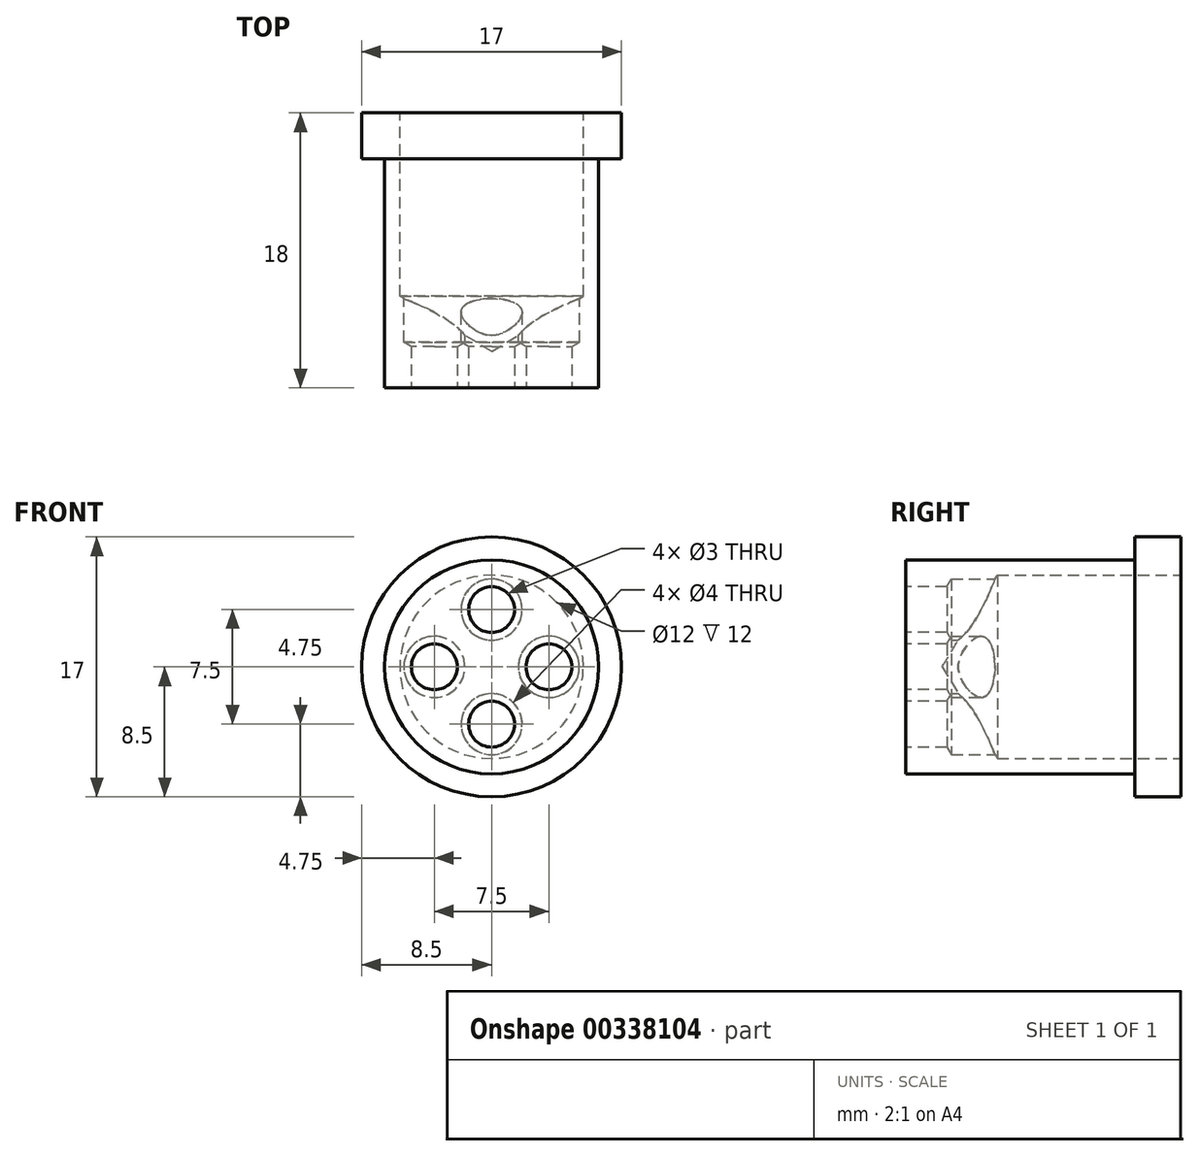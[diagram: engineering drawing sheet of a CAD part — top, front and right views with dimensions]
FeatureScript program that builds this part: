
annotation { "Feature Type Name" : "Feature", "Feature Type Description" : "" }
export const myFeature = defineFeature(function(context is Context, id is Id, definition is map)
    precondition{}
    {
        {
            var Q0;
            Q0=qCreatedBy(makeId("Front.planeOp"),FACE);
            var sketch = newSketch(context, id + "F0", { "sketchPlane" : qUnion([Q0])});
            skCircle(sketch, "E0", {"center": v(0, 0) * mm, "radius": 8.5 * mm});
            skSolve(sketch);
        }
        {
            var Q0;
            Q0=makeQuery(id+"F0.imprint","IMPRINT",FACE,{"disambiguationData":[TD([[makeQuery(id+"F0.imprint","IMPRINT",EDGE,{"derivedFrom":sQuery(id+"F0.wireOp",EDGE,"E0")}),1.0]])]});
            extrude(context, id + "F1", {"entities" : qUnion([Q0]), "depth" : 3 * mm});
        }
        {
            var Q0;
            Q0=makeQuery(id+"F1.opExtrude","CAP_FACE",FACE,{"disambiguationData":[OSD([sQuery(id+"F0.wireOp",EDGE,"E0")])],"isStart":false});
            var sketch = newSketch(context, id + "F2", { "sketchPlane" : qUnion([Q0])});
            skCircle(sketch, "E1", {"center": v(0, 0) * mm, "radius": 7 * mm});
            skSolve(sketch);
        }
        {
            var Q0;
            Q0=makeQuery(id+"F2.imprint","IMPRINT",FACE,{"disambiguationData":[TD([[makeQuery(id+"F2.imprint","IMPRINT",EDGE,{"derivedFrom":sQuery(id+"F2.wireOp",EDGE,"E1")}),1.0]])]});
            extrude(context, id + "F3", {"entities" : qUnion([Q0]), "operationType" : NewBodyOperationType.ADD, "depth" : 15 * mm});
        }
        {
            var Q0;
            Q0=makeQuery(id+"F3.opExtrude","CAP_FACE",FACE,{"disambiguationData":[OSD([sQuery(id+"F2.wireOp",EDGE,"E1")])],"isStart":false});
            var sketch = newSketch(context, id + "F4", { "sketchPlane" : qUnion([Q0])});
            skCircle(sketch, "E2", {"center": v(0, 3.75) * mm, "radius": 1.5 * mm});
            skCircle(sketch, "E3", {"center": v(-3.75, 0) * mm, "radius": 1.5 * mm});
            skCircle(sketch, "E4", {"center": v(0, -3.75) * mm, "radius": 1.5 * mm});
            skCircle(sketch, "E5", {"center": v(3.75, 0) * mm, "radius": 1.5 * mm});
            skSolve(sketch);
        }
        {
            var Q0;
            Q0=sQuery(id+"F4.wireOp",VERTEX,"E2.center");
            var Q1;
            Q1=sQuery(id+"F4.wireOp",VERTEX,"E5.center");
            var Q2;
            Q2=sQuery(id+"F4.wireOp",VERTEX,"E4.center");
            var Q3;
            Q3=sQuery(id+"F4.wireOp",VERTEX,"E3.center");
            var Q4;
            Q4=makeQuery(id+"F1.opExtrude","SWEPT_BODY",BODY,{"disambiguationData":[OSD([sQuery(id+"F0.wireOp",EDGE,"E0")])]});
            hole(context, id + "F5", {"style" : HoleStyle.SIMPLE, "endStyle" : HoleEndStyle.THROUGH, "holeDiameter" : 3 * mm, "tappedDepth" : 12 * mm, "tapClearance" : 3, "locations" : qUnion([Q0, Q1, Q2, Q3]), "scope" : qUnion([Q4])});
        }
        {
            var Q0;
            Q0=makeQuery(id+"F1.opExtrude","CAP_FACE",FACE,{"disambiguationData":[OSD([sQuery(id+"F0.wireOp",EDGE,"E0")])],"isStart":true});
            var sketch = newSketch(context, id + "F6", { "sketchPlane" : qUnion([Q0])});
            skCircle(sketch, "E6", {"center": v(0, 0) * mm, "radius": 6 * mm});
            skSolve(sketch);
        }
        {
            var Q0;
            Q0=sQuery(id+"F6.wireOp",VERTEX,"E6.center");
            var Q1;
            Q1=makeQuery(id+"F1.opExtrude","SWEPT_BODY",BODY,{"disambiguationData":[OSD([sQuery(id+"F0.wireOp",EDGE,"E0")])]});
            hole(context, id + "F7", {"style" : HoleStyle.SIMPLE, "endStyle" : HoleEndStyle.BLIND, "holeDiameter" : 12 * mm, "holeDepth" : 12 * mm, "tappedDepth" : 12 * mm, "tapClearance" : 3, "locations" : qUnion([Q0]), "scope" : qUnion([Q1])});
        }
        {
            var Q0;
            Q0=makeQuery(id+"F1.opExtrude","CAP_FACE",FACE,{"disambiguationData":[OSD([sQuery(id+"F0.wireOp",EDGE,"E0")])],"isStart":true});
            var sketch = newSketch(context, id + "F8", { "sketchPlane" : qUnion([Q0])});
            skCircle(sketch, "E7", {"center": v(3.75, 0) * mm, "radius": 2.25 * mm});
            skCircle(sketch, "E8", {"center": v(0, 3.75) * mm, "radius": 2.25 * mm});
            skCircle(sketch, "E9", {"center": v(-3.75, 0) * mm, "radius": 2.25 * mm});
            skCircle(sketch, "E10", {"center": v(0, -3.75) * mm, "radius": 2.25 * mm});
            skSolve(sketch);
        }
        {
            var Q0;
            Q0=sQuery(id+"F8.wireOp",VERTEX,"E8.center");
            var Q1;
            Q1=sQuery(id+"F8.wireOp",VERTEX,"E9.center");
            var Q2;
            Q2=sQuery(id+"F8.wireOp",VERTEX,"E7.center");
            var Q3;
            Q3=sQuery(id+"F8.wireOp",VERTEX,"E10.center");
            var Q4;
            Q4=makeQuery(id+"F1.opExtrude","SWEPT_BODY",BODY,{"disambiguationData":[OSD([sQuery(id+"F0.wireOp",EDGE,"E0")])]});
            hole(context, id + "F9", {"style" : HoleStyle.SIMPLE, "endStyle" : HoleEndStyle.BLIND, "holeDiameter" : 4 * mm, "holeDepth" : 15 * mm, "tappedDepth" : 12 * mm, "tapClearance" : 3, "startFromSketch" : true, "locations" : qUnion([Q0, Q1, Q2, Q3]), "scope" : qUnion([Q4])});
        }
    });
